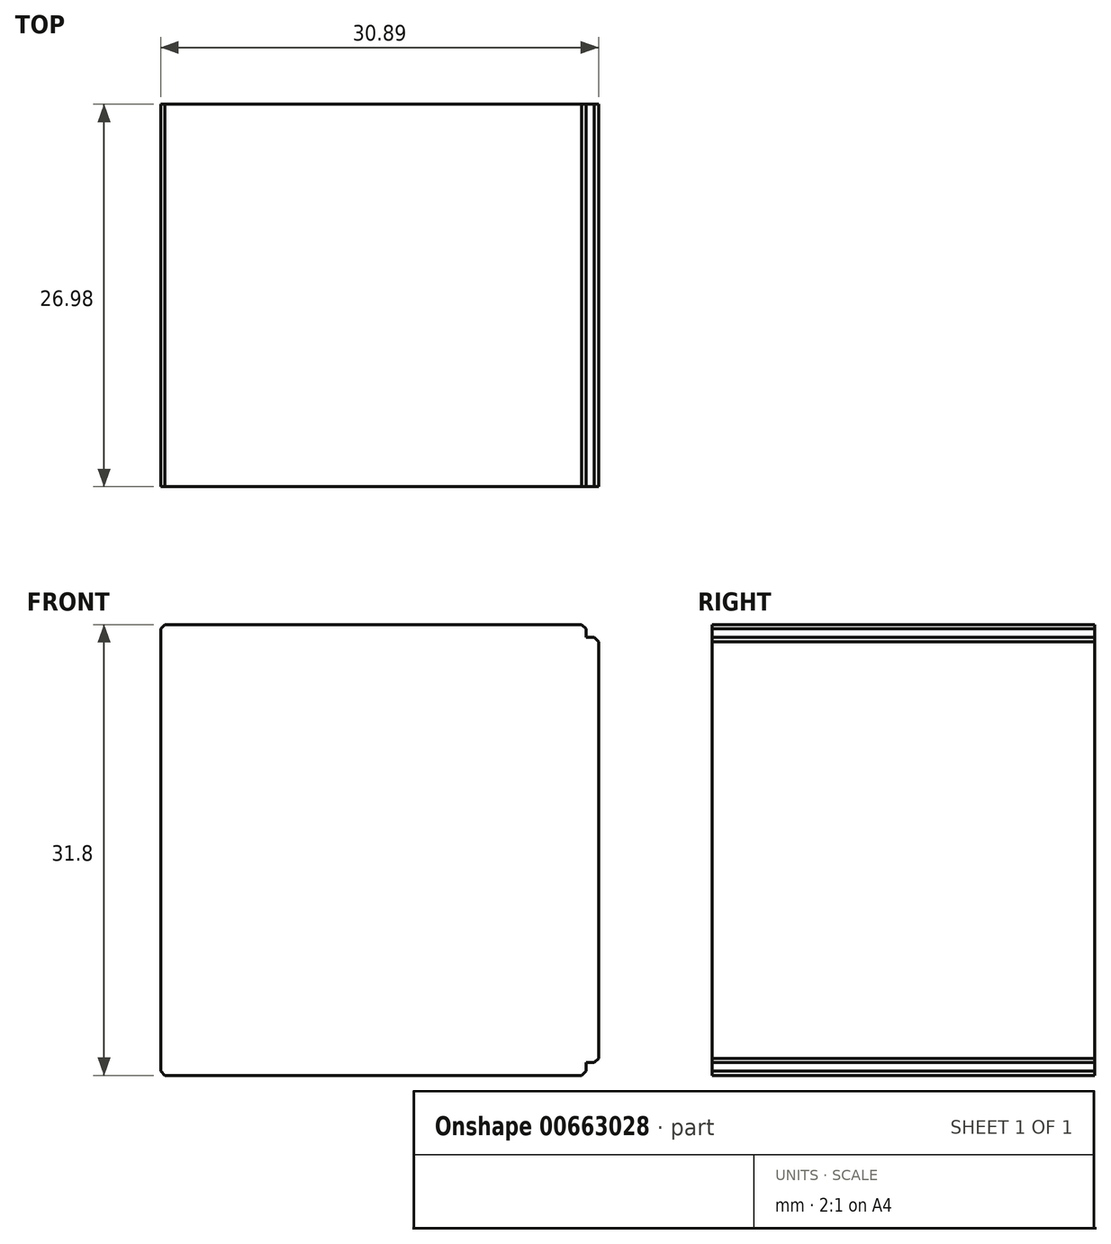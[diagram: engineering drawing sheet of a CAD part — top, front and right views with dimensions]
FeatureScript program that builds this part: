
annotation { "Feature Type Name" : "Feature", "Feature Type Description" : "" }
export const myFeature = defineFeature(function(context is Context, id is Id, definition is map)
    precondition{}
    {
        {
            var Q0;
            Q0=qCreatedBy(makeId("Front.planeOp"),FACE);
            var sketch = newSketch(context, id + "F0", { "sketchPlane" : qUnion([Q0])});
            skLineSegment(sketch, "E0", {"start": v(0, 0) * mm, "end": v(0, 31.2) * mm});
            skLineSegment(sketch, "E1", {"start": v(0, 31.2) * mm, "end": v(30, 31.2) * mm});
            skLineSegment(sketch, "E2", {"start": v(30, 31.2) * mm, "end": v(30, 30.6) * mm});
            skLineSegment(sketch, "E3", {"start": v(30, 30.6) * mm, "end": v(30.6, 30.6) * mm});
            skLineSegment(sketch, "E4", {"start": v(30.6, 30.6) * mm, "end": v(30.6, 0.6) * mm});
            skLineSegment(sketch, "E5", {"start": v(30.6, 0.6) * mm, "end": v(30, 0.6) * mm});
            skLineSegment(sketch, "E6", {"start": v(30, 0.6) * mm, "end": v(30, 0) * mm});
            skLineSegment(sketch, "E7", {"start": v(30, 0) * mm, "end": v(0, 0) * mm});
            skSolve(sketch);
        }
        {
            var Q0;
            Q0 = qSketchRegion(id + "F0", true);
            var Q1;
            Q1=makeQuery(id+"F0.imprint","IMPRINT",FACE,{"disambiguationData":[TD([[makeQuery(id+"F0.imprint","IMPRINT",EDGE,{"derivedFrom":sQuery(id+"F0.wireOp",EDGE,"E0")}),-1.0]])]});
            extrude(context, id + "F1", {"entities" : qUnion([Q0, Q1]), "depth" : 26.98 * mm, "offsetDistance" : 25 * mm});
        }
        {
            var Q0;
            Q0=makeQuery(id+"F1.opExtrude","CAP_FACE",FACE,{"disambiguationData":[OSD([sQuery(id+"F0.wireOp",EDGE,"E0"),sQuery(id+"F0.wireOp",EDGE,"E1"),sQuery(id+"F0.wireOp",EDGE,"E2"),sQuery(id+"F0.wireOp",EDGE,"E3"),sQuery(id+"F0.wireOp",EDGE,"E4"),sQuery(id+"F0.wireOp",EDGE,"E5"),sQuery(id+"F0.wireOp",EDGE,"E6"),sQuery(id+"F0.wireOp",EDGE,"E7")])],"isStart":false});
            var sketch = newSketch(context, id + "F2", { "sketchPlane" : qUnion([Q0])});
            skLineSegment(sketch, "E8", {"start": v(0.3, 31.2) * mm, "end": v(0.3, 31.5) * mm, "construction": true});
            skLineSegment(sketch, "E9", {"start": v(15, 31.2) * mm, "end": v(15, 0) * mm, "construction": true});
            skLineSegment(sketch, "E10.MirrorCS", {"start": v(29.7, 31.2) * mm, "end": v(29.7, 31.5) * mm, "construction": true});
            skLineSegment(sketch, "E11", {"start": v(0, 31.2) * mm, "end": v(0.3, 31.5) * mm});
            skLineSegment(sketch, "E12", {"start": v(29.7, 31.5) * mm, "end": v(30, 31.2) * mm});
            skLineSegment(sketch, "E13", {"start": v(0.3, 31.5) * mm, "end": v(29.7, 31.5) * mm});
            skLineSegment(sketch, "E14", {"start": v(0, 15.6) * mm, "end": v(30.6, 15.6) * mm, "construction": true});
            skLineSegment(sketch, "E15.MirrorCS", {"start": v(0, 0) * mm, "end": v(0.3, -0.3) * mm});
            skLineSegment(sketch, "E16.MirrorCS", {"start": v(0.3, -0.3) * mm, "end": v(29.7, -0.3) * mm});
            skLineSegment(sketch, "E17.MirrorCS", {"start": v(29.7, -0.3) * mm, "end": v(30, 0) * mm});
            skLineSegment(sketch, "E18", {"start": v(30.6, 30.3) * mm, "end": v(30.9, 30.3) * mm, "construction": true});
            skLineSegment(sketch, "E19.MirrorCS", {"start": v(30.6, 0.9) * mm, "end": v(30.9, 0.9) * mm, "construction": true});
            skLineSegment(sketch, "E20", {"start": v(30.6, 0.6) * mm, "end": v(30.9, 0.9) * mm});
            skLineSegment(sketch, "E21", {"start": v(30.9, 30.3) * mm, "end": v(30.9, 0.9) * mm});
            skLineSegment(sketch, "E22", {"start": v(30.9, 30.3) * mm, "end": v(30.6, 30.6) * mm});
            skSolve(sketch);
        }
        {
            var Q0;
            Q0=makeQuery(id+"F2.imprint","IMPRINT",FACE,{"disambiguationData":[TD([[makeQuery(id+"F2.imprint","IMPRINT",EDGE,{"derivedFrom":sQuery(id+"F2.wireOp",EDGE,"E11")}),-1.0]])]});
            var Q1;
            Q1=makeQuery(id+"F2.imprint","IMPRINT",FACE,{"disambiguationData":[TD([[makeQuery(id+"F2.imprint","IMPRINT",EDGE,{"derivedFrom":sQuery(id+"F2.wireOp",EDGE,"E20")}),1.0]])]});
            var Q2;
            Q2=makeQuery(id+"F2.imprint","IMPRINT",FACE,{"disambiguationData":[TD([[makeQuery(id+"F2.imprint","IMPRINT",EDGE,{"derivedFrom":sQuery(id+"F2.wireOp",EDGE,"E15.MirrorCS")}),1.0]])]});
            var Q3;
            Q3=makeQuery(id+"F1.opExtrude","CAP_FACE",FACE,{"disambiguationData":[OSD([sQuery(id+"F0.wireOp",EDGE,"E0"),sQuery(id+"F0.wireOp",EDGE,"E1"),sQuery(id+"F0.wireOp",EDGE,"E2"),sQuery(id+"F0.wireOp",EDGE,"E3"),sQuery(id+"F0.wireOp",EDGE,"E4"),sQuery(id+"F0.wireOp",EDGE,"E5"),sQuery(id+"F0.wireOp",EDGE,"E6"),sQuery(id+"F0.wireOp",EDGE,"E7")])],"isStart":true});
            extrude(context, id + "F3", {"entities" : qUnion([Q0, Q1, Q2]), "operationType" : NewBodyOperationType.ADD, "endBound" : BoundingType.UP_TO_SURFACE, "oppositeDirection" : true, "depth" : 25 * mm, "endBoundEntityFace" : qUnion([Q3]), "offsetDistance" : 25 * mm});
        }
    });
